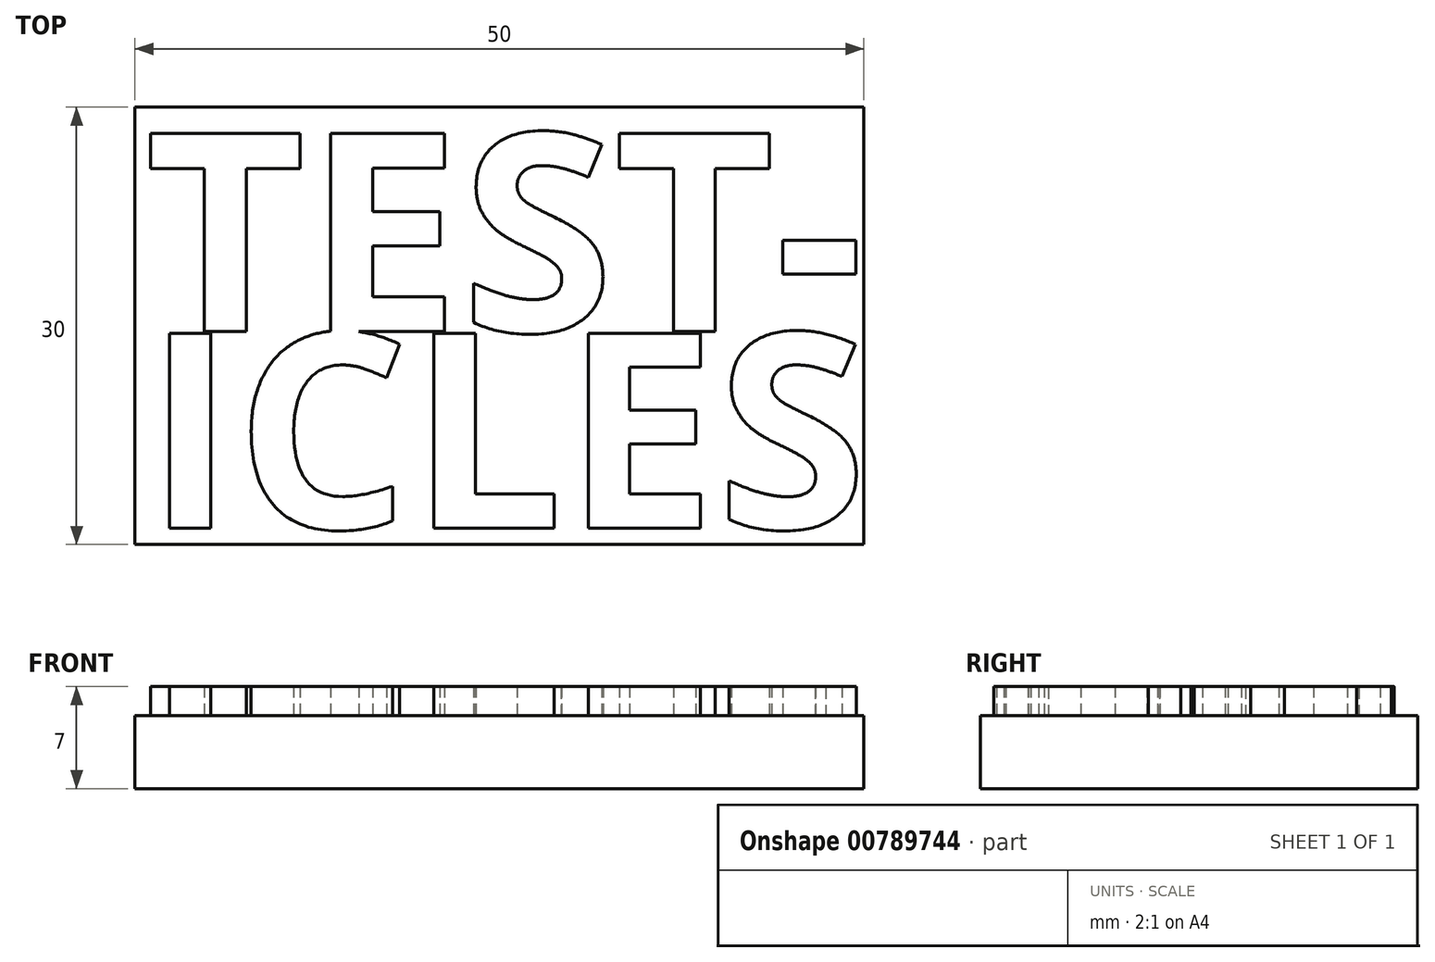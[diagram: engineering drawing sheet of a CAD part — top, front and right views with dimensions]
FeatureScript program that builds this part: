
annotation { "Feature Type Name" : "Feature", "Feature Type Description" : "" }
export const myFeature = defineFeature(function(context is Context, id is Id, definition is map)
    precondition{}
    {
        {
            var Q0;
            Q0=qCreatedBy(makeId("Top.planeOp"),FACE);
            var sketch = newSketch(context, id + "F0", { "sketchPlane" : qUnion([Q0])});
            skLineSegment(sketch, "E0.bottom", {"start": v(-29.78, 14.72) * mm, "end": v(20.22, 14.72) * mm});
            skLineSegment(sketch, "E0.top", {"start": v(-29.78, -15.28) * mm, "end": v(20.22, -15.28) * mm});
            skLineSegment(sketch, "E0.left", {"start": v(-29.78, 14.72) * mm, "end": v(-29.78, -15.28) * mm});
            skLineSegment(sketch, "E0.right", {"start": v(20.22, 14.72) * mm, "end": v(20.22, -15.28) * mm});
            skSolve(sketch);
        }
        {
            var Q0;
            Q0=makeQuery(id+"F0.imprint","IMPRINT",FACE,{"disambiguationData":[TD([[makeQuery(id+"F0.imprint","IMPRINT",EDGE,{"derivedFrom":sQuery(id+"F0.wireOp",EDGE,"E0.bottom")}),-1.0]])]});
            extrude(context, id + "F1", {"entities" : qUnion([Q0]), "depth" : 5 * mm, "offsetDistance" : 25 * mm});
        }
        {
            var Q0;
            Q0=makeQuery(id+"F1.opExtrude","CAP_FACE",FACE,{"disambiguationData":[OSD([sQuery(id+"F0.wireOp",EDGE,"E0.bottom"),sQuery(id+"F0.wireOp",EDGE,"E0.top"),sQuery(id+"F0.wireOp",EDGE,"E0.left"),sQuery(id+"F0.wireOp",EDGE,"E0.right")])],"isStart":false});
            var sketch = newSketch(context, id + "F2", { "sketchPlane" : qUnion([Q0])});
            skText(sketch, "E1", { "text": "TEST-", "fontName": "OpenSans-Bold.ttf"});
            skText(sketch, "E2", { "text": "ICLES", "fontName": "OpenSans-Bold.ttf"});
            const initialGuessF2  = {"E1": [-0.0291, -0.00068, 1, 0, 0.01371], "E2": [-0.0291, -0.01417, 1, 0, 0.01349]};
            skSetInitialGuess(sketch, initialGuessF2);
            skSolve(sketch);
        }
        {
            var Q0;
            Q0 = qSketchRegion(id + "F2", true);
            extrude(context, id + "F3", {"entities" : qUnion([Q0]), "operationType" : NewBodyOperationType.ADD, "depth" : 2 * mm, "offsetDistance" : 25 * mm});
        }
    });
